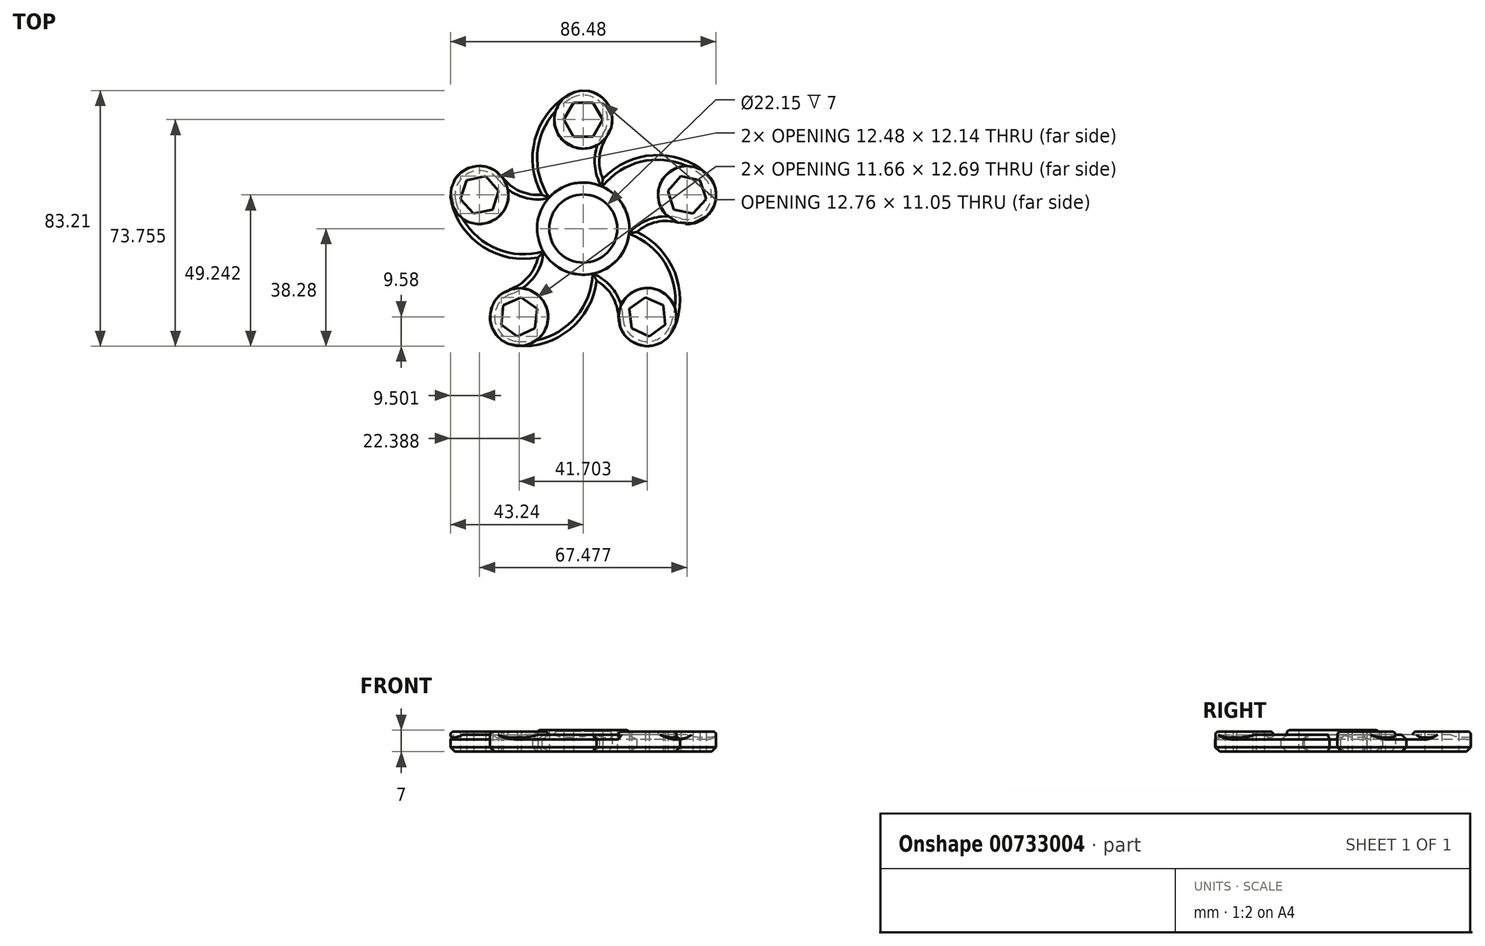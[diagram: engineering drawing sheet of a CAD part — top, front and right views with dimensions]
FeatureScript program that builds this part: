
annotation { "Feature Type Name" : "Feature", "Feature Type Description" : "" }
export const myFeature = defineFeature(function(context is Context, id is Id, definition is map)
    precondition{}
    {
        {
            var Q0;
            Q0=qCreatedBy(makeId("Top.planeOp"),FACE);
            var sketch = newSketch(context, id + "F0", { "sketchPlane" : qUnion([Q0])});
            skCircle(sketch, "E0", {"center": v(0, 0) * mm, "radius": 11.07 * mm});
            skCircle(sketch, "E1", {"center": v(0, 0) * mm, "radius": 15 * mm});
            skCircle(sketch, "E2.cCircle", {"center": v(0, 35.48) * mm, "radius": 5.53 * mm, "construction": true});
            skLineSegment(sketch, "E2.0", {"start": v(3.19, 29.95) * mm, "end": v(-3.19, 29.95) * mm});
            skLineSegment(sketch, "E2.1", {"start": v(-3.19, 29.95) * mm, "end": v(-6.38, 35.47) * mm});
            skLineSegment(sketch, "E2.2", {"start": v(-6.38, 35.47) * mm, "end": v(-3.19, 41) * mm});
            skLineSegment(sketch, "E2.3", {"start": v(-3.19, 41) * mm, "end": v(3.19, 41) * mm});
            skLineSegment(sketch, "E2.4", {"start": v(3.19, 41) * mm, "end": v(6.38, 35.48) * mm});
            skLineSegment(sketch, "E2.5", {"start": v(6.38, 35.48) * mm, "end": v(3.19, 29.95) * mm});
            skPoint(sketch, "E2.0.midPoint", {"position": v(0, 29.95) * mm});
            skCircle(sketch, "E3.1.0", {"center": v(33.74, 10.96) * mm, "radius": 5.53 * mm, "construction": true});
            skLineSegment(sketch, "E3.1.1", {"start": v(38, 15.7) * mm, "end": v(39.98, 9.64) * mm});
            skLineSegment(sketch, "E3.1.2", {"start": v(39.98, 9.64) * mm, "end": v(35.71, 4.9) * mm});
            skLineSegment(sketch, "E3.1.3", {"start": v(35.71, 4.9) * mm, "end": v(29.47, 6.22) * mm});
            skPoint(sketch, "E3.1.4", {"position": v(28.48, 9.26) * mm});
            skLineSegment(sketch, "E3.1.5", {"start": v(29.47, 6.22) * mm, "end": v(27.5, 12.29) * mm});
            skLineSegment(sketch, "E3.1.6", {"start": v(27.5, 12.29) * mm, "end": v(31.77, 17.03) * mm});
            skLineSegment(sketch, "E3.1.7", {"start": v(31.77, 17.03) * mm, "end": v(38, 15.7) * mm});
            skCircle(sketch, "E3.2.0", {"center": v(20.85, -28.7) * mm, "radius": 5.53 * mm, "construction": true});
            skLineSegment(sketch, "E3.2.1", {"start": v(26.68, -31.3) * mm, "end": v(21.52, -35.04) * mm});
            skLineSegment(sketch, "E3.2.2", {"start": v(21.52, -35.04) * mm, "end": v(15.7, -32.45) * mm});
            skLineSegment(sketch, "E3.2.3", {"start": v(15.7, -32.45) * mm, "end": v(15.02, -26.1) * mm});
            skPoint(sketch, "E3.2.4", {"position": v(17.6, -24.23) * mm});
            skLineSegment(sketch, "E3.2.5", {"start": v(15.02, -26.1) * mm, "end": v(20.18, -22.36) * mm});
            skLineSegment(sketch, "E3.2.6", {"start": v(20.18, -22.36) * mm, "end": v(26.01, -24.95) * mm});
            skLineSegment(sketch, "E3.2.7", {"start": v(26.01, -24.95) * mm, "end": v(26.68, -31.3) * mm});
            skCircle(sketch, "E3.3.0", {"center": v(-20.85, -28.7) * mm, "radius": 5.53 * mm, "construction": true});
            skLineSegment(sketch, "E3.3.1", {"start": v(-21.52, -35.04) * mm, "end": v(-26.68, -31.3) * mm});
            skLineSegment(sketch, "E3.3.2", {"start": v(-26.68, -31.3) * mm, "end": v(-26.01, -24.95) * mm});
            skLineSegment(sketch, "E3.3.3", {"start": v(-26.01, -24.95) * mm, "end": v(-20.18, -22.36) * mm});
            skPoint(sketch, "E3.3.4", {"position": v(-17.6, -24.23) * mm});
            skLineSegment(sketch, "E3.3.5", {"start": v(-20.18, -22.36) * mm, "end": v(-15.02, -26.1) * mm});
            skLineSegment(sketch, "E3.3.6", {"start": v(-15.02, -26.1) * mm, "end": v(-15.7, -32.45) * mm});
            skLineSegment(sketch, "E3.3.7", {"start": v(-15.7, -32.45) * mm, "end": v(-21.52, -35.04) * mm});
            skCircle(sketch, "E3.4.0", {"center": v(-33.74, 10.96) * mm, "radius": 5.53 * mm, "construction": true});
            skLineSegment(sketch, "E3.4.1", {"start": v(-39.98, 9.64) * mm, "end": v(-38, 15.7) * mm});
            skLineSegment(sketch, "E3.4.2", {"start": v(-38, 15.7) * mm, "end": v(-31.77, 17.03) * mm});
            skLineSegment(sketch, "E3.4.3", {"start": v(-31.77, 17.03) * mm, "end": v(-27.5, 12.29) * mm});
            skPoint(sketch, "E3.4.4", {"position": v(-28.48, 9.26) * mm});
            skLineSegment(sketch, "E3.4.5", {"start": v(-27.5, 12.29) * mm, "end": v(-29.47, 6.22) * mm});
            skLineSegment(sketch, "E3.4.6", {"start": v(-29.47, 6.22) * mm, "end": v(-35.71, 4.9) * mm});
            skLineSegment(sketch, "E3.4.7", {"start": v(-35.71, 4.9) * mm, "end": v(-39.98, 9.64) * mm});
            skLineSegment(sketch, "E3.anchor1", {"start": v(0, 0) * mm, "end": v(0, 29.95) * mm, "construction": true});
            skLineSegment(sketch, "E3.anchor2", {"start": v(0, 0) * mm, "end": v(-28.48, 9.26) * mm, "construction": true});
            skLineSegment(sketch, "E4", {"start": v(0, 0) * mm, "end": v(33.74, 10.96) * mm, "construction": true});
            skLineSegment(sketch, "E5", {"start": v(0, 0) * mm, "end": v(-20.85, -28.7) * mm, "construction": true});
            skLineSegment(sketch, "E6", {"start": v(20.85, -28.7) * mm, "end": v(0, 0) * mm, "construction": true});
            skCircle(sketch, "E7", {"center": v(0, 35.48) * mm, "radius": 9.45 * mm});
            skCircle(sketch, "E8.1.0", {"center": v(33.79, 10.93) * mm, "radius": 9.45 * mm});
            skCircle(sketch, "E8.2.0", {"center": v(20.88, -28.8) * mm, "radius": 9.45 * mm});
            skCircle(sketch, "E8.3.0", {"center": v(-20.88, -28.8) * mm, "radius": 9.45 * mm});
            skCircle(sketch, "E8.4.0", {"center": v(-33.79, 10.93) * mm, "radius": 9.45 * mm});
            skPoint(sketch, "E8.center", {"position": v(0, -0.05) * mm});
            skLineSegment(sketch, "E8.anchor1", {"start": v(0, -0.05) * mm, "end": v(0, 35.48) * mm, "construction": true});
            skLineSegment(sketch, "E8.anchor2", {"start": v(0, -0.05) * mm, "end": v(-33.79, 10.93) * mm, "construction": true});
            skArc(sketch, "E9", {"start": v(-4.95, 43.52) * mm, "mid": v(-15.72, 29) * mm, "end": v(-13.45, 11.05) * mm});
            skArc(sketch, "E10", {"start": v(7.77, 30.1) * mm, "mid": v(5.28, 23.3) * mm, "end": v(6.4, 16.17) * mm});
            skArc(sketch, "E11.1.0", {"start": v(-42.97, 8.7) * mm, "mid": v(-32.48, -6.02) * mm, "end": v(-14.71, -9.41) * mm});
            skArc(sketch, "E11.1.1", {"start": v(-26.27, 16.65) * mm, "mid": v(-20.59, 12.19) * mm, "end": v(-13.45, 11.05) * mm});
            skArc(sketch, "E11.2.0", {"start": v(-21.6, -38.21) * mm, "mid": v(-4.35, -32.78) * mm, "end": v(4.36, -16.93) * mm});
            skArc(sketch, "E11.2.1", {"start": v(-24, -19.87) * mm, "mid": v(-18, -15.85) * mm, "end": v(-14.71, -9.41) * mm});
            skArc(sketch, "E11.3.0", {"start": v(29.62, -32.4) * mm, "mid": v(29.79, -14.3) * mm, "end": v(17.4, -1.12) * mm});
            skArc(sketch, "E11.3.1", {"start": v(11.43, -29) * mm, "mid": v(9.46, -22.05) * mm, "end": v(4.36, -16.93) * mm});
            skArc(sketch, "E11.4.0", {"start": v(39.91, 18.12) * mm, "mid": v(22.76, 23.87) * mm, "end": v(6.4, 16.17) * mm});
            skArc(sketch, "E11.4.1", {"start": v(31.07, 1.88) * mm, "mid": v(23.85, 2.15) * mm, "end": v(17.4, -1.12) * mm});
            skPoint(sketch, "E12.orphan", {"position": v(10, 11.18) * mm});
            skPoint(sketch, "E13.orphan", {"position": v(4.76, 14.2) * mm});
            skPoint(sketch, "E14.orphan", {"position": v(15.03, -0.17) * mm});
            skPoint(sketch, "E15.orphan", {"position": v(13.77, -6.1) * mm});
            skPoint(sketch, "E16.orphan", {"position": v(4.53, -14.38) * mm});
            skPoint(sketch, "E17.orphan", {"position": v(-1.5, -15.01) * mm});
            skPoint(sketch, "E18.orphan", {"position": v(-12.23, -8.79) * mm});
            skPoint(sketch, "E19.orphan", {"position": v(-14.7, -3.26) * mm});
            skPoint(sketch, "E20.orphan", {"position": v(-7.59, 12.93) * mm});
            skPoint(sketch, "E21.orphan", {"position": v(-12.09, 8.88) * mm});
            skSolve(sketch);
        }
        {
            var Q0;
            Q0=makeQuery(id+"F0.imprint","IMPRINT",FACE,{"disambiguationData":[TD([[makeQuery(id+"F0.imprint","IMPRINT",EDGE,{"derivedFrom":sQuery(id+"F0.wireOp",EDGE,"E0")}),-1.0]])]});
            extrude(context, id + "F1", {"entities" : qUnion([Q0]), "depth" : 3.5 * mm, "offsetDistance" : 25 * mm, "hasSecondDirection" : true, "secondDirectionOppositeDirection" : true, "secondDirectionDepth" : 3.5 * mm});
        }
        {
            var Q0;
            Q0=makeQuery(id+"F0.imprint","IMPRINT",FACE,{"disambiguationData":[TD([[makeQuery(id+"F0.imprint","IMPRINT",EDGE,{"derivedFrom":sQuery(id+"F0.wireOp",EDGE,"E1")}),-1.0]])]});
            extrude(context, id + "F2", {"entities" : qUnion([Q0]), "operationType" : NewBodyOperationType.ADD, "depth" : 2 * mm, "offsetDistance" : 25 * mm, "hasSecondDirection" : true, "secondDirectionOppositeDirection" : true, "secondDirectionDepth" : 3.5 * mm});
        }
        {
            var Q0;
            Q0=makeQuery(id+"F0.imprint","IMPRINT",FACE,{"disambiguationData":[TD([[makeQuery(id+"F0.imprint","IMPRINT",EDGE,{"derivedFrom":sQuery(id+"F0.wireOp",EDGE,"E3.1.1")}),1.0]])]});
            var Q1;
            Q1=makeQuery(id+"F0.imprint","IMPRINT",FACE,{"disambiguationData":[TD([[makeQuery(id+"F0.imprint","IMPRINT",EDGE,{"derivedFrom":sQuery(id+"F0.wireOp",EDGE,"E3.4.1")}),1.0]])]});
            var Q2;
            Q2=makeQuery(id+"F0.imprint","IMPRINT",FACE,{"disambiguationData":[TD([[makeQuery(id+"F0.imprint","IMPRINT",EDGE,{"derivedFrom":sQuery(id+"F0.wireOp",EDGE,"E2.0")}),1.0]])]});
            var Q3;
            Q3=makeQuery(id+"F0.imprint","IMPRINT",FACE,{"disambiguationData":[TD([[makeQuery(id+"F0.imprint","IMPRINT",EDGE,{"derivedFrom":sQuery(id+"F0.wireOp",EDGE,"E3.3.1")}),1.0]])]});
            var Q4;
            Q4=makeQuery(id+"F0.imprint","IMPRINT",FACE,{"disambiguationData":[TD([[makeQuery(id+"F0.imprint","IMPRINT",EDGE,{"derivedFrom":sQuery(id+"F0.wireOp",EDGE,"E3.2.1")}),1.0]])]});
            extrude(context, id + "F3", {"entities" : qUnion([Q0, Q1, Q2, Q3, Q4]), "operationType" : NewBodyOperationType.ADD, "depth" : 3 * mm, "offsetDistance" : 25 * mm, "hasSecondDirection" : true, "secondDirectionOppositeDirection" : true, "secondDirectionDepth" : 3.5 * mm});
        }
        {
            var Q0;
            Q0=makeQuery(id+"F3.opExtrude","CAP_EDGE",EDGE,{"disambiguationData":[OSD([sQuery(id+"F0.wireOp",EDGE,"E8.2.0")])],"isStart":false});
            var Q1;
            Q1=makeQuery(id+"F3.opExtrude","CAP_EDGE",EDGE,{"disambiguationData":[OSD([sQuery(id+"F0.wireOp",EDGE,"E8.3.0")])],"isStart":false});
            var Q2;
            Q2=makeQuery(id+"F1.opExtrude","CAP_EDGE",EDGE,{"disambiguationData":[OSD([sQuery(id+"F0.wireOp",EDGE,"E1")])],"isStart":false});
            var Q3;
            Q3=makeQuery(id+"F3.opExtrude","CAP_EDGE",EDGE,{"disambiguationData":[OSD([sQuery(id+"F0.wireOp",EDGE,"E8.1.0")])],"isStart":false});
            var Q4;
            Q4=makeQuery(id+"F3.opExtrude","CAP_EDGE",EDGE,{"disambiguationData":[OSD([sQuery(id+"F0.wireOp",EDGE,"E7")])],"isStart":false});
            var Q5;
            Q5=makeQuery(id+"F3.opExtrude","CAP_EDGE",EDGE,{"disambiguationData":[OSD([sQuery(id+"F0.wireOp",EDGE,"E8.4.0")])],"isStart":false});
            fillet(context, id + "F4", {"entities" : qUnion([Q0, Q1, Q2, Q3, Q4, Q5]), "radius" : 1 * mm, "tangentPropagation" : true, "allowEdgeOverflow" : false});
        }
        {
            var Q0;
            Q0=makeQuery(id+"F2.opExtrude","CAP_EDGE",EDGE,{"disambiguationData":[OSD([sQuery(id+"F0.wireOp",EDGE,"E11.4.0")])],"isStart":true});
            var Q1;
            Q1=makeQuery(id+"F2.opExtrude","CAP_EDGE",EDGE,{"disambiguationData":[OSD([sQuery(id+"F0.wireOp",EDGE,"E10")])],"isStart":true});
            var Q2;
            Q2=makeQuery(id+"F3.opExtrude","CAP_EDGE",EDGE,{"disambiguationData":[OSD([sQuery(id+"F0.wireOp",EDGE,"E7")])],"isStart":true});
            var Q3;
            Q3=makeQuery(id+"F2.opExtrude","CAP_EDGE",EDGE,{"disambiguationData":[OSD([sQuery(id+"F0.wireOp",EDGE,"E9")])],"isStart":true});
            var Q4;
            Q4=makeQuery(id+"F2.opExtrude","CAP_EDGE",EDGE,{"disambiguationData":[OSD([sQuery(id+"F0.wireOp",EDGE,"E11.1.1")])],"isStart":true});
            var Q5;
            Q5=makeQuery(id+"F3.opExtrude","CAP_EDGE",EDGE,{"disambiguationData":[OSD([sQuery(id+"F0.wireOp",EDGE,"E8.4.0")])],"isStart":true});
            var Q6;
            Q6=makeQuery(id+"F2.opExtrude","CAP_EDGE",EDGE,{"disambiguationData":[OSD([sQuery(id+"F0.wireOp",EDGE,"E11.1.0")])],"isStart":true});
            var Q7;
            Q7=makeQuery(id+"F2.opExtrude","CAP_EDGE",EDGE,{"disambiguationData":[OSD([sQuery(id+"F0.wireOp",EDGE,"E11.2.1")])],"isStart":true});
            var Q8;
            Q8=makeQuery(id+"F3.opExtrude","CAP_EDGE",EDGE,{"disambiguationData":[OSD([sQuery(id+"F0.wireOp",EDGE,"E8.3.0")])],"isStart":true});
            var Q9;
            Q9=makeQuery(id+"F2.opExtrude","CAP_EDGE",EDGE,{"disambiguationData":[OSD([sQuery(id+"F0.wireOp",EDGE,"E11.2.0")])],"isStart":true});
            var Q10;
            Q10=makeQuery(id+"F2.opExtrude","CAP_EDGE",EDGE,{"disambiguationData":[OSD([sQuery(id+"F0.wireOp",EDGE,"E11.3.1")])],"isStart":true});
            var Q11;
            Q11=makeQuery(id+"F3.opExtrude","CAP_EDGE",EDGE,{"disambiguationData":[OSD([sQuery(id+"F0.wireOp",EDGE,"E8.2.0")])],"isStart":true});
            var Q12;
            Q12=makeQuery(id+"F2.opExtrude","CAP_EDGE",EDGE,{"disambiguationData":[OSD([sQuery(id+"F0.wireOp",EDGE,"E11.3.0")])],"isStart":true});
            var Q13;
            Q13=makeQuery(id+"F2.opExtrude","CAP_EDGE",EDGE,{"disambiguationData":[OSD([sQuery(id+"F0.wireOp",EDGE,"E11.4.1")])],"isStart":true});
            var Q14;
            Q14=makeQuery(id+"F3.opExtrude","CAP_EDGE",EDGE,{"disambiguationData":[OSD([sQuery(id+"F0.wireOp",EDGE,"E8.1.0")])],"isStart":true});
            chamfer(context, id + "F5", {"entities" : qUnion([Q0, Q1, Q2, Q3, Q4, Q5, Q6, Q7, Q8, Q9, Q10, Q11, Q12, Q13, Q14]), "width" : 1.5 * mm, "tangentPropagation" : true});
        }
        {
            var Q0;
            Q0=makeQuery(id+"F2.opExtrude","CAP_EDGE",EDGE,{"disambiguationData":[OSD([sQuery(id+"F0.wireOp",EDGE,"E11.1.1")])],"isStart":false});
            var Q1;
            Q1=makeQuery(id+"F2.opExtrude","CAP_EDGE",EDGE,{"disambiguationData":[OSD([sQuery(id+"F0.wireOp",EDGE,"E11.1.0")])],"isStart":false});
            var Q2;
            Q2=makeQuery(id+"F2.opExtrude","CAP_EDGE",EDGE,{"disambiguationData":[OSD([sQuery(id+"F0.wireOp",EDGE,"E11.2.1")])],"isStart":false});
            var Q3;
            Q3=makeQuery(id+"F2.opExtrude","CAP_EDGE",EDGE,{"disambiguationData":[OSD([sQuery(id+"F0.wireOp",EDGE,"E9")])],"isStart":false});
            var Q4;
            Q4=makeQuery(id+"F2.opExtrude","CAP_EDGE",EDGE,{"disambiguationData":[OSD([sQuery(id+"F0.wireOp",EDGE,"E10")])],"isStart":false});
            var Q5;
            Q5=makeQuery(id+"F2.opExtrude","CAP_EDGE",EDGE,{"disambiguationData":[OSD([sQuery(id+"F0.wireOp",EDGE,"E11.4.0")])],"isStart":false});
            var Q6;
            Q6=makeQuery(id+"F2.opExtrude","CAP_EDGE",EDGE,{"disambiguationData":[OSD([sQuery(id+"F0.wireOp",EDGE,"E11.4.1")])],"isStart":false});
            var Q7;
            Q7=makeQuery(id+"F2.opExtrude","CAP_EDGE",EDGE,{"disambiguationData":[OSD([sQuery(id+"F0.wireOp",EDGE,"E11.3.0")])],"isStart":false});
            var Q8;
            Q8=makeQuery(id+"F2.opExtrude","CAP_EDGE",EDGE,{"disambiguationData":[OSD([sQuery(id+"F0.wireOp",EDGE,"E11.3.1")])],"isStart":false});
            var Q9;
            Q9=makeQuery(id+"F2.opExtrude","CAP_EDGE",EDGE,{"disambiguationData":[OSD([sQuery(id+"F0.wireOp",EDGE,"E11.2.0")])],"isStart":false});
            chamfer(context, id + "F6", {"entities" : qUnion([Q0, Q1, Q2, Q3, Q4, Q5, Q6, Q7, Q8, Q9]), "width" : 1.5 * mm, "tangentPropagation" : true});
        }
    });
